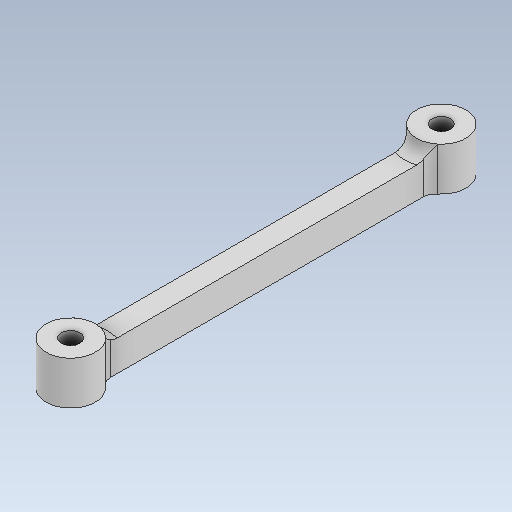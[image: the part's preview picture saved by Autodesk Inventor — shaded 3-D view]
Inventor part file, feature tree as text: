
AUTODESK INVENTOR PART (.ipt)
format: ipt  version: 2020 (Build 240168000, 168)  size: 119,808 bytes
history: native  units: mm
features: other x3, sketch x3
ambient origin geometry x8: Origin, YZ Plane, XZ Plane, XY Plane, X Axis, Y Axis, Z Axis, Center Point
bodies: Solid1 (feature_tree)
feature tree (6):
  other  "leg_link_3_m.ipt"
  other  "Solid1::leg_link_3_m.ipt"
  other  "TaggingFeature1"
  sketch  "Sketch1"  dims[d0=10.0mm]
  sketch  "Sketch2"
  sketch  "Sketch3"
